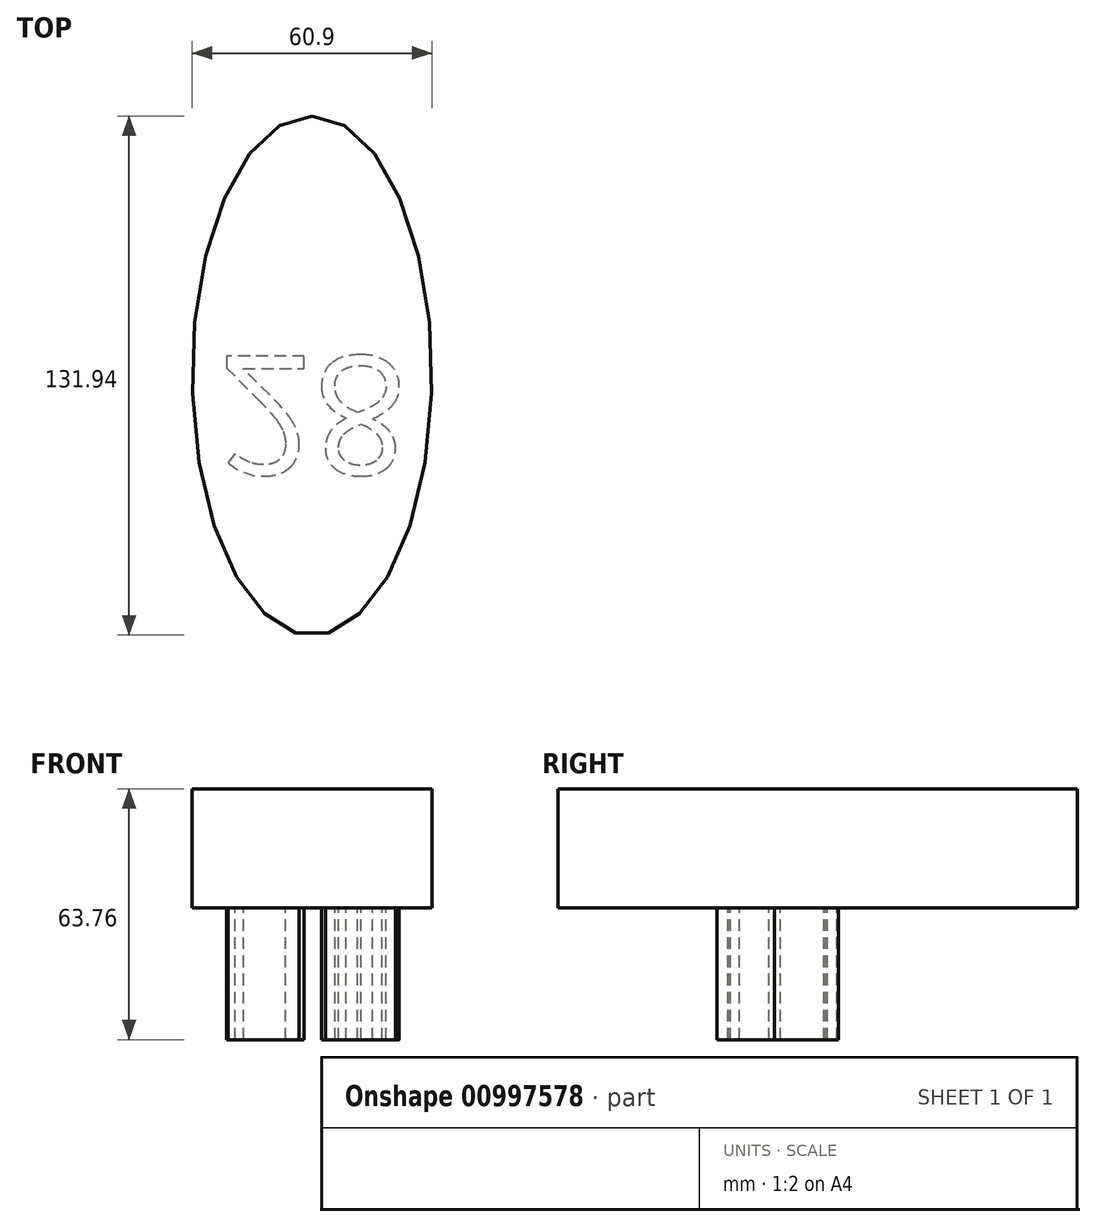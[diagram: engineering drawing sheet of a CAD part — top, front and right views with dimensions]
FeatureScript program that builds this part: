
annotation { "Feature Type Name" : "Feature", "Feature Type Description" : "" }
export const myFeature = defineFeature(function(context is Context, id is Id, definition is map)
    precondition{}
    {
        {
            var Q0;
            Q0=qCreatedBy(makeId("Top.planeOp"),FACE);
            var sketch = newSketch(context, id + "F0", { "sketchPlane" : qUnion([Q0])});
            skEllipse(sketch, "E0", {"center": v(0, 0) * mm, "majorRadius": 65.97 * mm, "minorRadius": 30.45 * mm, "majorAxis": v(0, 1)});
            skSolve(sketch);
        }
        {
            var Q0;
            Q0=makeQuery(id+"F0.imprint","IMPRINT",FACE,{"disambiguationData":[TD([[makeQuery(id+"F0.imprint","IMPRINT",EDGE,{"derivedFrom":sQuery(id+"F0.wireOp",EDGE,"E0")}),1.0]])]});
            extrude(context, id + "F1", {"entities" : qUnion([Q0]), "depth" : 30.23 * mm, "offsetDistance" : 25.4 * mm});
        }
        {
            var Q0;
            Q0=makeQuery(id+"F1.opExtrude","CAP_FACE",FACE,{"disambiguationData":[OSD([sQuery(id+"F0.wireOp",EDGE,"E0")])],"isStart":false});
            var sketch = newSketch(context, id + "F2", { "sketchPlane" : qUnion([Q0])});
            skSolve(sketch);
        }
        {
            var Q0;
            Q0=makeQuery(id+"F1.opExtrude","CAP_FACE",FACE,{"disambiguationData":[OSD([sQuery(id+"F0.wireOp",EDGE,"E0")])],"isStart":true});
            var sketch = newSketch(context, id + "F3", { "sketchPlane" : qUnion([Q0])});
            skText(sketch, "E1", { "text": "28", "fontName": "OpenSans-Regular.ttf"});
            const initialGuessF3  = {"E1": [-0.02379, -0.0049, 1, 0, 0.0303]};
            skSetInitialGuess(sketch, initialGuessF3);
            skSolve(sketch);
        }
        {
            var Q0;
            Q0 = qSketchRegion(id + "F3", true);
            extrude(context, id + "F4", {"entities" : qUnion([Q0]), "operationType" : NewBodyOperationType.ADD, "depth" : 33.53 * mm, "offsetDistance" : 25.4 * mm});
        }
    });
